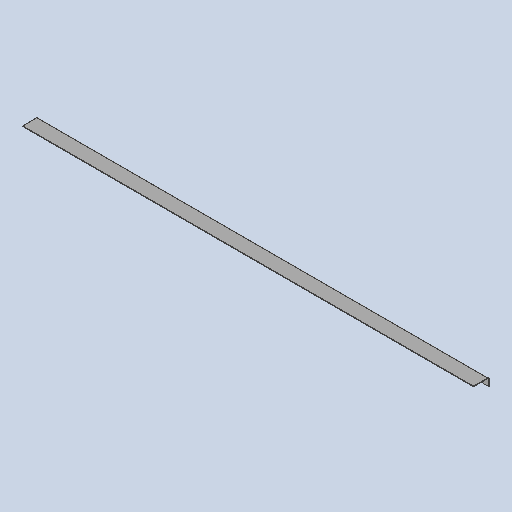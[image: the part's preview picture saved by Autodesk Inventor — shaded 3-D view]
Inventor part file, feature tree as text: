
AUTODESK INVENTOR PART (.ipt)
format: ipt  version: 2025 (Build 290162010, 162A)  size: 162,304 bytes
history: native  units: mm
features: other x5, sheet_metal_op x4, sketch x2, mirror x1
ambient origin geometry x8: Origin, YZ Plane, XZ Plane, XY Plane, X Axis, Y Axis, Z Axis, Center Point
bodies: Body1 (feature_tree)
feature tree (12):
  other  "BSH 035 divider 1"
  sheet_metal_op  "Face2"
  sheet_metal_op  "Flange3"
  other  "Corner Chamfer2"
  mirror  "Mirror2"
  sketch  "Sketch5"  dims[d26=1200.0mm]
  other  "Plate4"
  sketch  "Sketch6"  dims[d27=2897.0mm d28=3.0mm d29=53.0mm d30=947.0mm d31=150.0mm d32=103.0mm d36=100.0mm d37=100.0mm d38=100.0mm d39=850.0mm d40=873.5mm d41=873.5mm d42=3.0mm d43=1.5mm d44=6.0mm d45=5.0mm d46=40.0mm d47=90.0deg d48=5.0mm d49=12.0mm d50=3.0mm d51=5.0mm d52=6.0mm d53=6.0mm d54=45.0deg d55=80.0mm]
  other  "Plate5"
  sheet_metal_op  "Bend3"
  sheet_metal_op  "Corner3"
  other  "Definition1"
